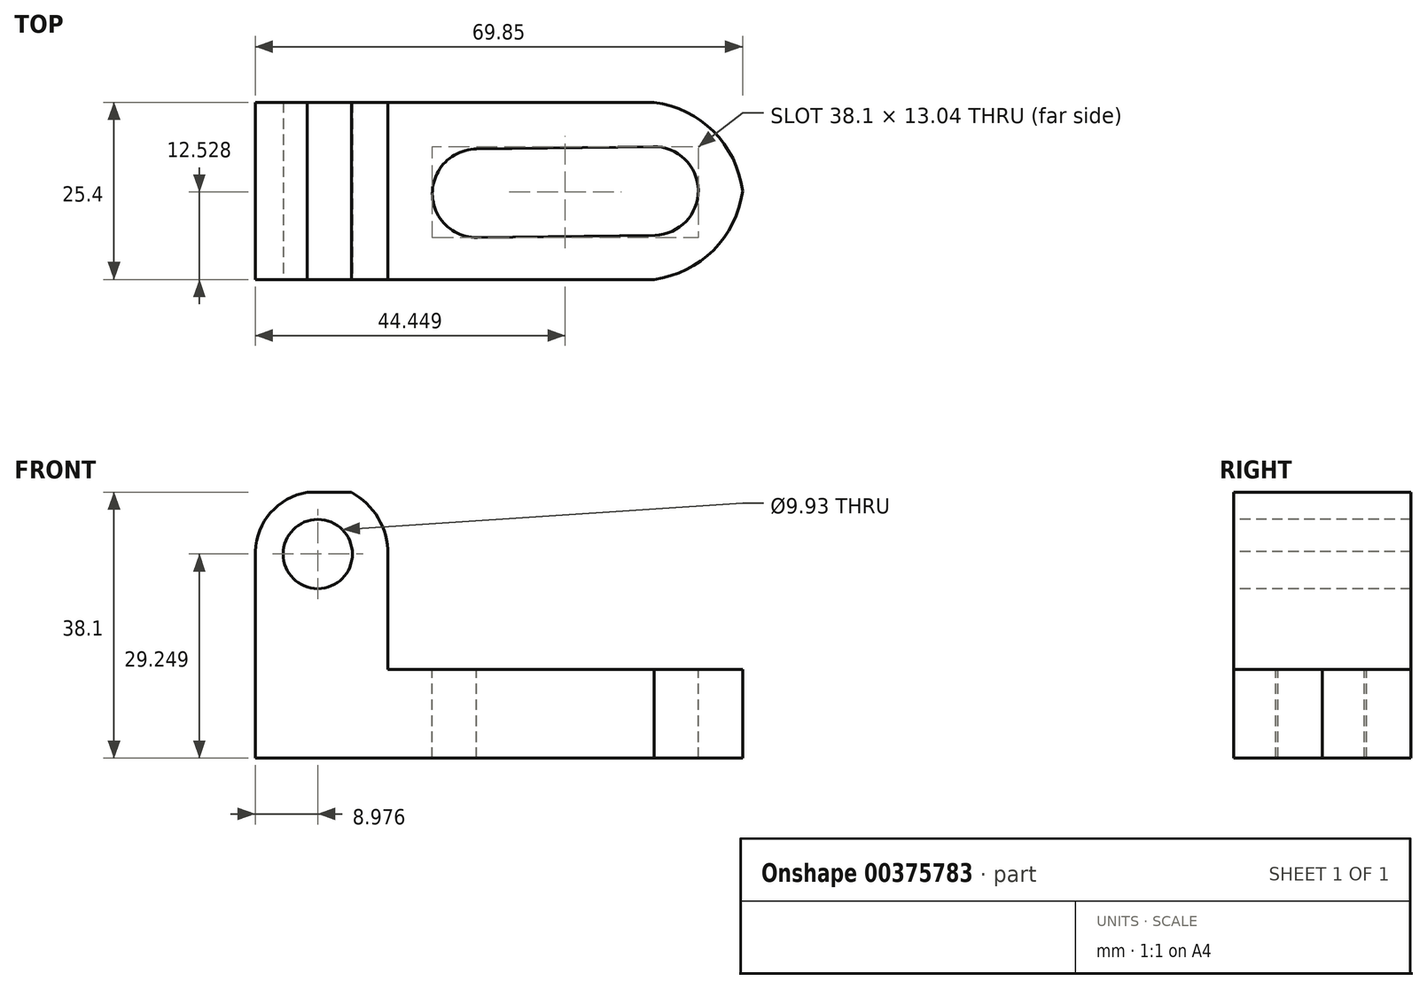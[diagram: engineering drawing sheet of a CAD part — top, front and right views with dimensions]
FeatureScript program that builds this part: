
annotation { "Feature Type Name" : "Feature", "Feature Type Description" : "" }
export const myFeature = defineFeature(function(context is Context, id is Id, definition is map)
    precondition{}
    {
        {
            var Q0;
            Q0=qCreatedBy(makeId("Front.planeOp"),FACE);
            var sketch = newSketch(context, id + "F0", { "sketchPlane" : qUnion([Q0])});
            skLineSegment(sketch, "E0", {"start": v(-69.85, 0) * mm, "end": v(0, 0) * mm});
            skLineSegment(sketch, "E1", {"start": v(0, 0) * mm, "end": v(0, 12.7) * mm});
            skLineSegment(sketch, "E2", {"start": v(0, 12.7) * mm, "end": v(-50.8, 12.7) * mm});
            skLineSegment(sketch, "E3", {"start": v(-50.8, 12.7) * mm, "end": v(-50.8, 38.1) * mm});
            skLineSegment(sketch, "E4", {"start": v(-50.8, 38.1) * mm, "end": v(-69.85, 38.1) * mm});
            skLineSegment(sketch, "E5", {"start": v(-69.85, 38.1) * mm, "end": v(-69.85, 0) * mm});
            skSolve(sketch);
        }
        {
            var Q0;
            Q0=makeQuery(id+"F0.imprint","IMPRINT",FACE,{"disambiguationData":[TD([[makeQuery(id+"F0.imprint","IMPRINT",EDGE,{"derivedFrom":sQuery(id+"F0.wireOp",EDGE,"E0")}),1.0]])]});
            extrude(context, id + "F1", {"entities" : qUnion([Q0]), "depth" : 25.4 * mm});
        }
        {
            var Q0;
            Q0=makeQuery(id+"F1.opExtrude","SWEPT_FACE",FACE,{"disambiguationData":[OSD([sQuery(id+"F0.wireOp",EDGE,"E2")])]});
            var sketch = newSketch(context, id + "F2", { "sketchPlane" : qUnion([Q0])});
            skArc(sketch, "E6", {"start": v(0, -12.7) * mm, "mid": v(-4.17, -4.17) * mm, "end": v(-12.7, 0) * mm});
            skArc(sketch, "E7", {"start": v(-12.7, -25.4) * mm, "mid": v(-4.2, -21.2) * mm, "end": v(0, -12.7) * mm});
            skLineSegment(sketch, "E8", {"start": v(-12.7, -25.4) * mm, "end": v(0, -25.4) * mm});
            skLineSegment(sketch, "E9", {"start": v(0, -25.4) * mm, "end": v(0, -12.7) * mm});
            skLineSegment(sketch, "E10", {"start": v(0, -12.7) * mm, "end": v(0, 0) * mm});
            skLineSegment(sketch, "E11", {"start": v(0, 0) * mm, "end": v(-12.7, 0) * mm});
            skSolve(sketch);
        }
        {
            var Q0;
            Q0=makeQuery(id+"F2.imprint","IMPRINT",FACE,{"disambiguationData":[TD([[makeQuery(id+"F2.imprint","IMPRINT",EDGE,{"derivedFrom":sQuery(id+"F2.wireOp",EDGE,"E6")}),-1.0]])]});
            var Q1;
            Q1=makeQuery(id+"F2.imprint","IMPRINT",FACE,{"disambiguationData":[TD([[makeQuery(id+"F2.imprint","IMPRINT",EDGE,{"derivedFrom":sQuery(id+"F2.wireOp",EDGE,"E7")}),-1.0]])]});
            extrude(context, id + "F3", {"entities" : qUnion([Q0, Q1]), "operationType" : NewBodyOperationType.REMOVE, "oppositeDirection" : true, "depth" : 12.7 * mm});
        }
        {
            var Q0;
            Q0=makeQuery(id+"F1.opExtrude","SWEPT_FACE",FACE,{"disambiguationData":[OSD([sQuery(id+"F0.wireOp",EDGE,"E2")])]});
            var sketch = newSketch(context, id + "F4", { "sketchPlane" : qUnion([Q0])});
            skCircle(sketch, "E12", {"center": v(-38.1, -13.04) * mm, "radius": 6.35 * mm});
            skCircle(sketch, "E13", {"center": v(-12.7, -12.7) * mm, "radius": 6.35 * mm});
            skLineSegment(sketch, "E14", {"start": v(-38.1, -6.7) * mm, "end": v(-12.7, -6.35) * mm});
            skLineSegment(sketch, "E15", {"start": v(-12.53, -19.05) * mm, "end": v(-38.1, -19.4) * mm});
            skSolve(sketch);
        }
        {
            var Q0;
            {var subQ0=sQuery(id+"F4.wireOp",EDGE,"E12");var subQ1=makeQuery(id+"F4.imprint","INTERSECT",VERTEX,{"derivedFrom":[subQ0,sQuery(id+"F4.wireOp",EDGE,"E14")]});Q0=makeQuery(id+"F4.imprint","IMPRINT",FACE,{"disambiguationData":[TD([[makeQuery(id+"F4.imprint","IMPRINT",EDGE,{"disambiguationData":[TD([[subQ1,-1.0]])],"derivedFrom":subQ0}),1.0]])]});}
            var Q1;
            {var subQ0=sQuery(id+"F4.wireOp",EDGE,"E14");var subQ1=sQuery(id+"F4.wireOp",EDGE,"E12");var subQ2=makeQuery(id+"F4.imprint","INTERSECT",VERTEX,{"derivedFrom":[subQ1,subQ0]});Q1=makeQuery(id+"F4.imprint","IMPRINT",FACE,{"disambiguationData":[TD([[makeQuery(id+"F4.imprint","IMPRINT",EDGE,{"disambiguationData":[TD([[subQ2,1.0]])],"derivedFrom":subQ1}),-1.0]])]});}
            var Q2;
            {var subQ0=sQuery(id+"F4.wireOp",EDGE,"E13");var subQ1=makeQuery(id+"F4.imprint","INTERSECT",VERTEX,{"derivedFrom":[subQ0,sQuery(id+"F4.wireOp",EDGE,"E14")]});Q2=makeQuery(id+"F4.imprint","IMPRINT",FACE,{"disambiguationData":[TD([[makeQuery(id+"F4.imprint","IMPRINT",EDGE,{"disambiguationData":[TD([[subQ1,-1.0]])],"derivedFrom":subQ0}),1.0]])]});}
            extrude(context, id + "F5", {"entities" : qUnion([Q0, Q1, Q2]), "operationType" : NewBodyOperationType.REMOVE, "oppositeDirection" : true, "depth" : 12.7 * mm});
        }
        {
            var Q0;
            Q0=makeQuery(id+"F1.opExtrude","CAP_FACE",FACE,{"disambiguationData":[OSD([sQuery(id+"F0.wireOp",EDGE,"E0"),sQuery(id+"F0.wireOp",EDGE,"E1"),sQuery(id+"F0.wireOp",EDGE,"E2"),sQuery(id+"F0.wireOp",EDGE,"E3"),sQuery(id+"F0.wireOp",EDGE,"E4"),sQuery(id+"F0.wireOp",EDGE,"E5")])],"isStart":false});
            var sketch = newSketch(context, id + "F6", { "sketchPlane" : qUnion([Q0])});
            skArc(sketch, "E16", {"start": v(-69.85, 28.88) * mm, "mid": v(-67.87, 34.9) * mm, "end": v(-62.41, 38.1) * mm});
            skArc(sketch, "E17", {"start": v(-50.8, 29.25) * mm, "mid": v(-52.21, 34.4) * mm, "end": v(-56.06, 38.1) * mm});
            skLineSegment(sketch, "E18", {"start": v(-50.8, 29.25) * mm, "end": v(-50.8, 38.1) * mm});
            skLineSegment(sketch, "E19", {"start": v(-50.8, 38.1) * mm, "end": v(-56.06, 38.1) * mm});
            skLineSegment(sketch, "E20", {"start": v(-69.85, 28.88) * mm, "end": v(-69.85, 38.1) * mm});
            skLineSegment(sketch, "E21", {"start": v(-69.85, 38.1) * mm, "end": v(-62.41, 38.1) * mm});
            skSolve(sketch);
        }
        {
            var Q0;
            {var subQ0=sQuery(id+"F6.wireOp",EDGE,"E21");Q0=makeQuery(id+"F6.imprint","IMPRINT",FACE,{"disambiguationData":[TD([[makeQuery(id+"F6.imprint","IMPRINT",EDGE,{"derivedFrom":subQ0}),1.0]])]});}
            var Q1;
            Q1=makeQuery(id+"F6.imprint","IMPRINT",FACE,{"disambiguationData":[TD([[makeQuery(id+"F6.imprint","IMPRINT",EDGE,{"derivedFrom":sQuery(id+"F6.wireOp",EDGE,"E17")}),-1.0]])]});
            extrude(context, id + "F7", {"entities" : qUnion([Q0, Q1]), "operationType" : NewBodyOperationType.REMOVE, "oppositeDirection" : true, "depth" : 25.4 * mm});
        }
        {
            var Q0;
            Q0=makeQuery(id+"F1.opExtrude","CAP_FACE",FACE,{"disambiguationData":[OSD([sQuery(id+"F0.wireOp",EDGE,"E0"),sQuery(id+"F0.wireOp",EDGE,"E1"),sQuery(id+"F0.wireOp",EDGE,"E2"),sQuery(id+"F0.wireOp",EDGE,"E3"),sQuery(id+"F0.wireOp",EDGE,"E4"),sQuery(id+"F0.wireOp",EDGE,"E5")])],"isStart":false});
            var sketch = newSketch(context, id + "F8", { "sketchPlane" : qUnion([Q0])});
            skCircle(sketch, "E22", {"center": v(-60.87, 29.25) * mm, "radius": 4.96 * mm});
            skSolve(sketch);
        }
        {
            var Q0;
            Q0=makeQuery(id+"F8.imprint","IMPRINT",FACE,{"disambiguationData":[TD([[makeQuery(id+"F8.imprint","IMPRINT",EDGE,{"derivedFrom":sQuery(id+"F8.wireOp",EDGE,"E22")}),1.0]])]});
            extrude(context, id + "F9", {"entities" : qUnion([Q0]), "operationType" : NewBodyOperationType.REMOVE, "oppositeDirection" : true, "depth" : 25.4 * mm});
        }
    });
